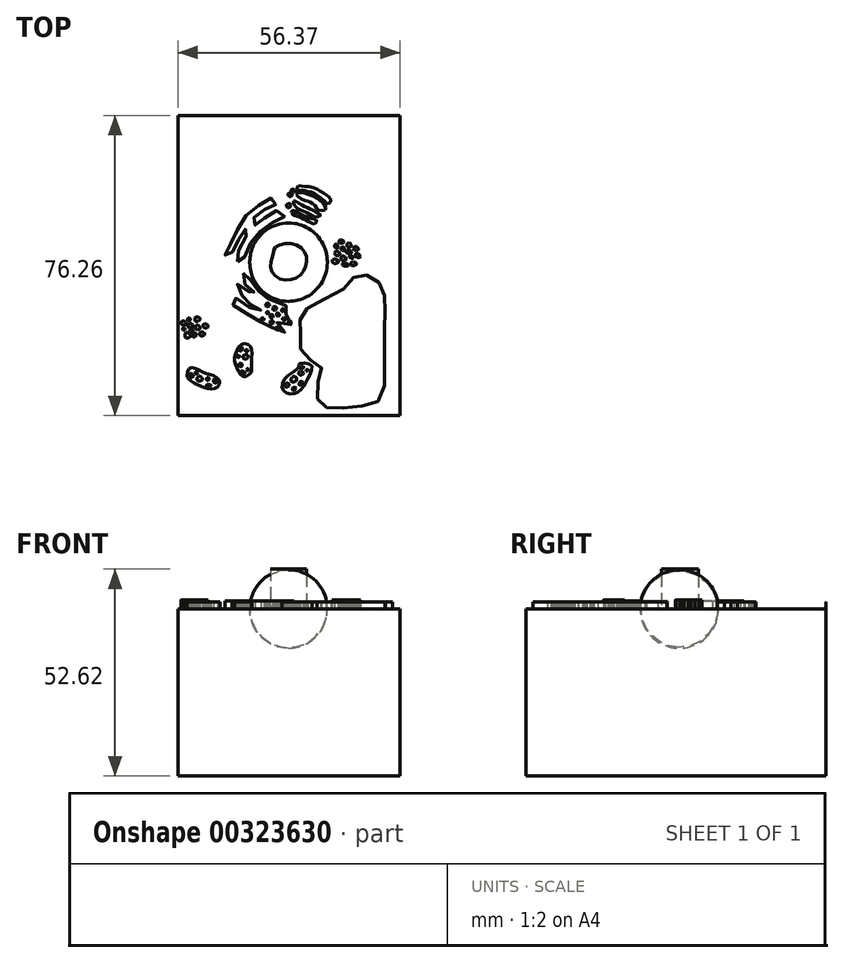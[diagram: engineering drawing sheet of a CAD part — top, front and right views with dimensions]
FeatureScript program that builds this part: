
annotation { "Feature Type Name" : "Feature", "Feature Type Description" : "" }
export const myFeature = defineFeature(function(context is Context, id is Id, definition is map)
    precondition{}
    {
        {
            var Q0;
            Q0=qCreatedBy(makeId("Front.planeOp"),FACE);
            var sketch = newSketch(context, id + "F0", { "sketchPlane" : qUnion([Q0])});
            skLineSegment(sketch, "E0", {"start": v(0, 0) * mm, "end": v(56.37, 0) * mm});
            skLineSegment(sketch, "E1", {"start": v(56.37, 0) * mm, "end": v(56.37, 42.46) * mm});
            skLineSegment(sketch, "E2", {"start": v(56.37, 42.46) * mm, "end": v(0, 42.46) * mm});
            skLineSegment(sketch, "E3", {"start": v(0, 42.46) * mm, "end": v(0, 0) * mm});
            skSolve(sketch);
        }
        {
            var Q0;
            Q0 = qSketchRegion(id + "F0", true);
            extrude(context, id + "F1", {"entities" : qUnion([Q0]), "depth" : 76.2 * mm});
        }
        {
            var Q0;
            Q0=makeQuery(id+"F1.opExtrude","SWEPT_FACE",FACE,{"disambiguationData":[OSD([sQuery(id+"F0.wireOp",EDGE,"E2")])]});
            var sketch = newSketch(context, id + "F2", { "sketchPlane" : qUnion([Q0])});
            skLineSegment(sketch, "E4", {"start": v(18.2, -37.24) * mm, "end": v(37.91, -37.24) * mm});
            skArc(sketch, "E5", {"start": v(37.91, -37.24) * mm, "mid": v(28.06, -27.5) * mm, "end": v(18.2, -37.24) * mm});
            skSolve(sketch);
        }
        {
            var Q0;
            Q0 = qSketchRegion(id + "F2", true);
            var Q1;
            Q1=sQuery(id+"F2.wireOp",EDGE,"E4");
            revolve(context, id + "F3", {"entities" : qUnion([Q0]), "axis" : qUnion([Q1]), "revolveType" : RevolveType.FULL});
        }
        {
            var Q0;
            Q0=makeQuery(id+"F1.opExtrude","SWEPT_FACE",FACE,{"disambiguationData":[OSD([sQuery(id+"F0.wireOp",EDGE,"E2")])]});
            var sketch = newSketch(context, id + "F4", { "sketchPlane" : qUnion([Q0])});
            skLineSegment(sketch, "E6", {"start": v(23.53, -36.84) * mm, "end": v(33.16, -36.84) * mm});
            skArc(sketch, "E7", {"start": v(33.16, -36.84) * mm, "mid": v(28.34, -32.03) * mm, "end": v(23.53, -36.84) * mm});
            skSolve(sketch);
        }
        {
            var Q0;
            Q0=sQuery(id+"F4.wireOp",EDGE,"E6");
            var Q1;
            Q1=sQuery(id+"F4.wireOp",EDGE,"E7");
            var Q2;
            Q2=makeQuery(id+"F3.opRevolve","SWEPT_FACE",FACE,{"disambiguationData":[OSD([sQuery(id+"F2.wireOp",EDGE,"E5")])]});
            revolve(context, id + "F5", {"bodyType" : ToolBodyType.SURFACE, "surfaceEntities" : qUnion([Q0, Q1]), "axis" : qUnion([Q2]), "revolveType" : RevolveType.FULL});
        }
        {
            var Q0;
            Q0=makeQuery(id+"F1.opExtrude","SWEPT_FACE",FACE,{"disambiguationData":[OSD([sQuery(id+"F0.wireOp",EDGE,"E2")])]});
            var sketch = newSketch(context, id + "F6", { "sketchPlane" : qUnion([Q0])});
            skFitSpline(sketch, "E8", {"points": [v(31.3, -19.52) * mm, v(34.38, -20.54) * mm, v(36.71, -22.14) * mm, v(37.51, -23.8) * mm, v(35.92, -24.05) * mm, v(34.75, -22.9) * mm, v(33.42, -21.92) * mm, v(31.77, -21.36) * mm, v(30.08, -19.97) * mm, v(30.5, -19.6) * mm, v(31.3, -19.52) * mm]});
            skFitSpline(sketch, "E9", {"points": [v(29.34, -21.68) * mm, v(31.26, -22.56) * mm, v(33.27, -23.6) * mm, v(35.23, -24.57) * mm, v(36.13, -25.3) * mm, v(35.33, -25.73) * mm, v(33.38, -25.13) * mm, v(32.04, -24.33) * mm, v(30.14, -23.49) * mm, v(29.34, -21.68) * mm]});
            skFitSpline(sketch, "E10", {"points": [v(29.72, -24.3) * mm, v(32.06, -25.46) * mm, v(34.16, -26.22) * mm, v(35.13, -26.54) * mm, v(34.7, -27.46) * mm, v(32.96, -26.83) * mm, v(30.75, -25.78) * mm, v(28.88, -24.77) * mm, v(28.96, -24.15) * mm, v(29.72, -24.3) * mm]});
            skFitSpline(sketch, "E11", {"points": [v(28.03, -19.78) * mm, v(28.28, -20.58) * mm, v(28.97, -20.07) * mm, v(28.03, -19.78) * mm]});
            skFitSpline(sketch, "E12", {"points": [v(27.61, -22.56) * mm, v(28.58, -22.53) * mm, v(28.3, -23.34) * mm, v(27.65, -23.2) * mm, v(27.61, -22.56) * mm]});
            skSolve(sketch);
        }
        {
            var Q0;
            Q0=makeQuery(id+"F6.imprint","IMPRINT",FACE,{"disambiguationData":[TD([[makeQuery(id+"F6.imprint","IMPRINT",EDGE,{"derivedFrom":sQuery(id+"F6.wireOp",EDGE,"E8")}),-1.0]])]});
            var Q1;
            Q1=makeQuery(id+"F6.imprint","IMPRINT",FACE,{"disambiguationData":[TD([[makeQuery(id+"F6.imprint","IMPRINT",EDGE,{"derivedFrom":sQuery(id+"F6.wireOp",EDGE,"E11")}),1.0]])]});
            var Q2;
            Q2=makeQuery(id+"F6.imprint","IMPRINT",FACE,{"disambiguationData":[TD([[makeQuery(id+"F6.imprint","IMPRINT",EDGE,{"derivedFrom":sQuery(id+"F6.wireOp",EDGE,"E10")}),-1.0]])]});
            var Q3;
            Q3=makeQuery(id+"F6.imprint","IMPRINT",FACE,{"disambiguationData":[TD([[makeQuery(id+"F6.imprint","IMPRINT",EDGE,{"derivedFrom":sQuery(id+"F6.wireOp",EDGE,"E9")}),-1.0]])]});
            var Q4;
            Q4=makeQuery(id+"F6.imprint","IMPRINT",FACE,{"disambiguationData":[TD([[makeQuery(id+"F6.imprint","IMPRINT",EDGE,{"derivedFrom":sQuery(id+"F6.wireOp",EDGE,"E12")}),-1.0]])]});
            extrude(context, id + "F7", {"entities" : qUnion([Q0, Q1, Q2, Q3, Q4]), "operationType" : NewBodyOperationType.ADD, "depth" : 1.78 * mm});
        }
        {
            var Q0;
            Q0=makeQuery(id+"F1.opExtrude","SWEPT_FACE",FACE,{"disambiguationData":[OSD([sQuery(id+"F0.wireOp",EDGE,"E2")])]});
            var sketch = newSketch(context, id + "F8", { "sketchPlane" : qUnion([Q0])});
            skFitSpline(sketch, "E13", {"points": [v(2.83, -64.3) * mm, v(2.4, -66.39) * mm, v(3.72, -67.72) * mm, v(5.38, -68.57) * mm, v(7.66, -69.4) * mm, v(9.46, -69.28) * mm, v(10.62, -67.74) * mm, v(9.1, -66.1) * mm, v(6.66, -65.34) * mm, v(4.44, -64.22) * mm, v(2.83, -64.3) * mm]});
            skFitSpline(sketch, "E14", {"points": [v(3.1, -65.6) * mm, v(3.22, -66.46) * mm, v(3.92, -66.02) * mm, v(3.48, -65.63) * mm, v(3.1, -65.6) * mm]});
            skFitSpline(sketch, "E15", {"points": [v(5.34, -66.2) * mm, v(4.77, -67.1) * mm, v(5.58, -67.42) * mm, v(6.18, -66.88) * mm, v(5.34, -66.2) * mm]});
            skFitSpline(sketch, "E16", {"points": [v(7.3, -66.67) * mm, v(7.3, -67.22) * mm, v(7.87, -67.02) * mm, v(7.71, -66.56) * mm, v(7.3, -66.67) * mm]});
            skFitSpline(sketch, "E17", {"points": [v(7.18, -68.5) * mm, v(7.77, -68.98) * mm, v(8.33, -68.56) * mm, v(7.8, -68.27) * mm, v(7.18, -68.5) * mm]});
            skFitSpline(sketch, "E18", {"points": [v(9.23, -66.88) * mm, v(9.02, -67.65) * mm, v(9.68, -67.88) * mm, v(9.97, -67.49) * mm, v(9.23, -66.88) * mm]});
            skFitSpline(sketch, "E19", {"points": [v(4.46, -65.05) * mm, v(4.57, -65.6) * mm, v(5.02, -65.33) * mm, v(4.77, -65.04) * mm, v(4.46, -65.05) * mm]});
            skFitSpline(sketch, "E20", {"points": [v(30.66, -63.92) * mm, v(27.48, -66.45) * mm, v(26.61, -69.5) * mm, v(28.81, -70.7) * mm, v(31.28, -69.48) * mm, v(33.02, -66.64) * mm, v(33.78, -63.35) * mm, v(30.7, -63.13) * mm, v(30.66, -63.92) * mm]});
            skFitSpline(sketch, "E21", {"points": [v(27.32, -68.2) * mm, v(27.35, -68.96) * mm, v(28.19, -68.62) * mm, v(27.85, -67.95) * mm, v(27.32, -68.2) * mm]});
            skFitSpline(sketch, "E22", {"points": [v(28.93, -66.47) * mm, v(28.82, -67.5) * mm, v(29.9, -67.45) * mm, v(30, -66.49) * mm, v(28.93, -66.47) * mm]});
            skFitSpline(sketch, "E23", {"points": [v(29.3, -69.83) * mm, v(29.91, -69.13) * mm, v(29.17, -69.16) * mm, v(29.06, -69.7) * mm, v(29.3, -69.83) * mm]});
            skFitSpline(sketch, "E24", {"points": [v(30.95, -67.67) * mm, v(30.86, -68.46) * mm, v(31.67, -68.1) * mm, v(31.42, -67.53) * mm, v(30.95, -67.67) * mm]});
            skFitSpline(sketch, "E25", {"points": [v(16.06, -58.2) * mm, v(14.67, -60.31) * mm, v(14.38, -62.5) * mm, v(15.41, -64.97) * mm, v(16.66, -66.29) * mm, v(18.52, -65.34) * mm, v(18.58, -63.17) * mm, v(18.77, -60.38) * mm, v(18.05, -58.27) * mm, v(16.06, -58.2) * mm]});
            skFitSpline(sketch, "E26", {"points": [v(15.76, -59.01) * mm, v(15.53, -59.64) * mm, v(16.1, -59.68) * mm, v(16.39, -59.1) * mm, v(15.76, -59.01) * mm]});
            skFitSpline(sketch, "E27", {"points": [v(17.36, -59.46) * mm, v(17.14, -59.85) * mm, v(17.71, -59.79) * mm, v(17.36, -59.46) * mm]});
            skFitSpline(sketch, "E28", {"points": [v(15.08, -60.93) * mm, v(15.12, -61.37) * mm, v(15.66, -61.2) * mm, v(15.08, -60.93) * mm]});
            skFitSpline(sketch, "E29", {"points": [v(17.03, -60.75) * mm, v(16.43, -61.42) * mm, v(16.89, -61.85) * mm, v(17.63, -61.6) * mm, v(17.78, -60.93) * mm, v(17.03, -60.75) * mm]});
            skFitSpline(sketch, "E30", {"points": [v(15.45, -63.06) * mm, v(16.28, -63.18) * mm, v(15.9, -63.77) * mm, v(15.45, -63.06) * mm]});
            skFitSpline(sketch, "E31", {"points": [v(17.58, -64.2) * mm, v(17.53, -64.73) * mm, v(17.97, -64.65) * mm, v(17.58, -64.2) * mm]});
            skFitSpline(sketch, "E32", {"points": [v(15.99, -64.92) * mm, v(16.15, -65.6) * mm, v(17, -65.35) * mm, v(15.99, -64.92) * mm]});
            skFitSpline(sketch, "E33", {"points": [v(30.95, -64.97) * mm, v(30.78, -65.78) * mm, v(31.82, -65.53) * mm, v(30.95, -64.97) * mm]});
            skFitSpline(sketch, "E34", {"points": [v(32.78, -64.46) * mm, v(32.56, -64.86) * mm, v(33.06, -64.73) * mm, v(32.78, -64.46) * mm]});
            skFitSpline(sketch, "E35", {"points": [v(31.32, -63.72) * mm, v(31.1, -64.27) * mm, v(31.93, -64.02) * mm, v(31.32, -63.72) * mm]});
            skSolve(sketch);
        }
        {
            var Q0;
            Q0 = qSketchRegion(id + "F8", true);
            extrude(context, id + "F9", {"entities" : qUnion([Q0]), "operationType" : NewBodyOperationType.ADD, "depth" : 1.78 * mm});
        }
        {
            var Q0;
            {var subQ1=sQuery(id+"F0.wireOp",EDGE,"E2");var subQ2=sQuery(id+"F0.wireOp",EDGE,"E1");Q0=makeQuery(id+"F9.boolean.opBoolean","SPLIT",FACE,{"disambiguationData":[TD([makeQuery(id+"F1.opExtrude","SWEPT_FACE",FACE,{"disambiguationData":[OSD([subQ2])]})])],"derivedFrom":makeQuery(id+"F1.opExtrude","SWEPT_FACE",FACE,{"disambiguationData":[OSD([subQ1])]})});}
            var sketch = newSketch(context, id + "F10", { "sketchPlane" : qUnion([Q0])});
            skFitSpline(sketch, "E36", {"points": [v(27.47, -50.37) * mm, v(28.2, -49.17) * mm, v(28.12, -48.16) * mm, v(26.8, -48.59) * mm, v(25.74, -48.68) * mm, v(25.5, -48.16) * mm, v(25.63, -47.5) * mm, v(24.86, -47.37) * mm, v(23.2, -46.81) * mm, v(22.66, -46.21) * mm, v(21.56, -45.4) * mm, v(20.63, -44.72) * mm, v(19.42, -43.5) * mm, v(18.64, -42.5) * mm, v(18.38, -41.47) * mm, v(17.9, -40.74) * mm, v(17.1, -40.1) * mm, v(16.55, -40.23) * mm, v(16.22, -40.98) * mm, v(16.46, -42.12) * mm, v(17.53, -43.19) * mm, v(18.47, -43.48) * mm, v(19.06, -44.67) * mm, v(19.59, -45.3) * mm, v(18.87, -45.96) * mm, v(17.95, -44.74) * mm, v(16.21, -43.7) * mm, v(15.38, -42.7) * mm, v(14.56, -43.76) * mm, v(15.46, -45.02) * mm, v(16.83, -46.19) * mm, v(17.94, -47.4) * mm, v(18.13, -47.86) * mm, v(19.5, -48.17) * mm, v(20.7, -48.36) * mm, v(20.95, -49.63) * mm, v(19.82, -50.39) * mm, v(18.34, -48.9) * mm, v(16.22, -47.83) * mm, v(14.73, -46.46) * mm, v(14.02, -45.55) * mm, v(13.72, -47.46) * mm, v(15.07, -48.9) * mm, v(16.73, -49.62) * mm, v(18.6, -51.47) * mm, v(20.61, -52.54) * mm, v(22.01, -52.3) * mm, v(23.11, -53.17) * mm, v(24.1, -54.15) * mm, v(25.64, -55.27) * mm, v(27.06, -55.02) * mm, v(26.22, -53.87) * mm, v(24.87, -52.75) * mm, v(26.37, -52.59) * mm, v(27.7, -53.01) * mm, v(28.9, -52.99) * mm, v(29.37, -51.91) * mm, v(27.47, -50.37) * mm]});
            skFitSpline(sketch, "E37", {"points": [v(25, -50.23) * mm, v(25.73, -50.45) * mm, v(25.37, -51) * mm, v(25, -50.23) * mm]});
            skFitSpline(sketch, "E38", {"points": [v(26.6, -51.4) * mm, v(26.78, -52.02) * mm, v(27.35, -51.69) * mm, v(26.6, -51.4) * mm]});
            skFitSpline(sketch, "E39", {"points": [v(23.4, -52.26) * mm, v(23.65, -52.93) * mm, v(24.19, -52.36) * mm, v(23.4, -52.26) * mm]});
            skFitSpline(sketch, "E40", {"points": [v(24.06, -51.25) * mm, v(23.83, -50.57) * mm, v(23.33, -51.17) * mm, v(24.06, -51.25) * mm]});
            skFitSpline(sketch, "E41", {"points": [v(26.6, -49.07) * mm, v(26.32, -49.61) * mm, v(26.96, -49.8) * mm, v(26.85, -49.26) * mm, v(26.6, -49.07) * mm]});
            skFitSpline(sketch, "E42", {"points": [v(24.82, -53.84) * mm, v(24.99, -54.41) * mm, v(25.59, -54.15) * mm, v(24.82, -53.84) * mm]});
            skFitSpline(sketch, "E43", {"points": [v(24.58, -48.45) * mm, v(24.09, -49.28) * mm, v(25, -49.1) * mm, v(24.58, -48.45) * mm]});
            skFitSpline(sketch, "E44", {"points": [v(22.74, -49.75) * mm, v(22.5, -50.26) * mm, v(23, -50.16) * mm, v(22.74, -49.75) * mm]});
            skFitSpline(sketch, "E45", {"points": [v(21.24, -51.47) * mm, v(21.17, -51.93) * mm, v(21.89, -51.7) * mm, v(21.24, -51.47) * mm]});
            skFitSpline(sketch, "E46", {"points": [v(22.8, -47.58) * mm, v(22.27, -48.29) * mm, v(23.16, -48.4) * mm, v(22.8, -47.58) * mm]});
            skFitSpline(sketch, "E47", {"points": [v(28.2, -52.13) * mm, v(28.2, -52.59) * mm, v(28.73, -52.44) * mm, v(28.2, -52.13) * mm]});
            skSolve(sketch);
        }
        {
            var Q0;
            Q0 = qSketchRegion(id + "F10", true);
            extrude(context, id + "F11", {"entities" : qUnion([Q0]), "operationType" : NewBodyOperationType.ADD, "depth" : 2.03 * mm});
        }
        {
            var Q0;
            {var subQ6=sQuery(id+"F0.wireOp",EDGE,"E2");var subQ7=sQuery(id+"F0.wireOp",EDGE,"E1");var subQ12=makeQuery(id+"F1.opExtrude","SWEPT_FACE",FACE,{"disambiguationData":[OSD([subQ7])]});Q0=makeQuery(id+"F11.boolean.opBoolean","SPLIT",FACE,{"disambiguationData":[TD([subQ12])],"derivedFrom":makeQuery(id+"F9.boolean.opBoolean","SPLIT",FACE,{"disambiguationData":[TD([subQ12])],"derivedFrom":makeQuery(id+"F1.opExtrude","SWEPT_FACE",FACE,{"disambiguationData":[OSD([subQ6])]})})});}
            var sketch = newSketch(context, id + "F12", { "sketchPlane" : qUnion([Q0])});
            skFitSpline(sketch, "E48", {"points": [v(40.12, -32.66) * mm, v(39.83, -33.41) * mm, v(40.65, -33.51) * mm, v(40.12, -32.66) * mm]});
            skFitSpline(sketch, "E49", {"points": [v(40.07, -34.4) * mm, v(40, -35.49) * mm, v(41.12, -35.19) * mm, v(40.07, -34.4) * mm]});
            skFitSpline(sketch, "E50", {"points": [v(41.75, -33.37) * mm, v(41.44, -34.06) * mm, v(42.34, -34.14) * mm, v(41.75, -33.37) * mm]});
            skFitSpline(sketch, "E51", {"points": [v(41.14, -31.56) * mm, v(41.02, -32.31) * mm, v(42.09, -32.15) * mm, v(41.14, -31.56) * mm]});
            skFitSpline(sketch, "E52", {"points": [v(43.4, -32.3) * mm, v(42.92, -33.18) * mm, v(43.9, -33.19) * mm, v(43.4, -32.3) * mm]});
            skFitSpline(sketch, "E53", {"points": [v(43.08, -34.15) * mm, v(42.76, -34.83) * mm, v(44.1, -34.89) * mm, v(43.08, -34.15) * mm]});
            skFitSpline(sketch, "E54", {"points": [v(41.86, -35.72) * mm, v(41.42, -36.57) * mm, v(42.7, -36.5) * mm, v(41.86, -35.72) * mm]});
            skFitSpline(sketch, "E55", {"points": [v(44.59, -36.17) * mm, v(43.66, -35.57) * mm, v(43.65, -36.01) * mm, v(44.59, -36.17) * mm]});
            skFitSpline(sketch, "E56", {"points": [v(45.01, -33.23) * mm, v(44.56, -34) * mm, v(45.8, -34) * mm, v(45.01, -33.23) * mm]});
            skFitSpline(sketch, "E57", {"points": [v(39.28, -36.6) * mm, v(39.6, -37.55) * mm, v(40.76, -36.97) * mm, v(39.28, -36.6) * mm]});
            skFitSpline(sketch, "E58", {"points": [v(45.19, -34.98) * mm, v(45.3, -35.88) * mm, v(46.3, -35.83) * mm, v(45.19, -34.98) * mm]});
            skFitSpline(sketch, "E59", {"points": [v(41.88, -37.5) * mm, v(41.97, -38.11) * mm, v(43.29, -37.98) * mm, v(41.88, -37.5) * mm]});
            skFitSpline(sketch, "E60", {"points": [v(44.25, -37.17) * mm, v(44, -38.05) * mm, v(45.32, -37.7) * mm, v(44.25, -37.17) * mm]});
            skFitSpline(sketch, "E61", {"points": [v(2.93, -52.8) * mm, v(2.62, -53.79) * mm, v(3.8, -53.38) * mm, v(2.93, -52.8) * mm]});
            skFitSpline(sketch, "E62", {"points": [v(4.91, -53.2) * mm, v(4.49, -54.22) * mm, v(5.53, -54.15) * mm, v(4.91, -53.2) * mm]});
            skFitSpline(sketch, "E63", {"points": [v(2.03, -55.1) * mm, v(2, -56.46) * mm, v(3.15, -55.94) * mm, v(2.03, -55.1) * mm]});
            skFitSpline(sketch, "E64", {"points": [v(4.06, -55.2) * mm, v(3.75, -56.19) * mm, v(4.68, -55.67) * mm, v(4.06, -55.2) * mm]});
            skFitSpline(sketch, "E65", {"points": [v(5.95, -54.92) * mm, v(5.53, -55.8) * mm, v(6.74, -55.65) * mm, v(5.95, -54.92) * mm]});
            skFitSpline(sketch, "E66", {"points": [v(6.72, -52.9) * mm, v(6.46, -53.77) * mm, v(7.65, -53.59) * mm, v(6.72, -52.9) * mm]});
            skFitSpline(sketch, "E67", {"points": [v(5.6, -51.66) * mm, v(4.52, -51.2) * mm, v(4.46, -52.24) * mm, v(5.6, -51.66) * mm]});
            skFitSpline(sketch, "E68", {"points": [v(2.66, -51.4) * mm, v(2.52, -52) * mm, v(3.16, -51.83) * mm, v(2.66, -51.4) * mm]});
            skFitSpline(sketch, "E69", {"points": [v(1.34, -53.92) * mm, v(1.2, -54.4) * mm, v(1.78, -54.25) * mm, v(1.34, -53.92) * mm]});
            skFitSpline(sketch, "E70", {"points": [v(1.05, -52.22) * mm, v(0.79, -52.9) * mm, v(1.96, -53.12) * mm, v(1.84, -52.45) * mm, v(1.05, -52.22) * mm]});
            skFitSpline(sketch, "E71", {"points": [v(3.04, -54.42) * mm, v(3.13, -54.93) * mm, v(3.62, -54.83) * mm, v(3.8, -54.3) * mm, v(3.19, -54.37) * mm, v(3.04, -54.42) * mm]});
            skSolve(sketch);
        }
        {
            var Q0;
            Q0 = qSketchRegion(id + "F12", true);
            extrude(context, id + "F13", {"entities" : qUnion([Q0]), "operationType" : NewBodyOperationType.ADD, "depth" : 2.3 * mm});
        }
        {
            var Q0;
            {var subQ6=sQuery(id+"F0.wireOp",EDGE,"E2");var subQ7=sQuery(id+"F0.wireOp",EDGE,"E1");var subQ12=makeQuery(id+"F1.opExtrude","SWEPT_FACE",FACE,{"disambiguationData":[OSD([subQ7])]});Q0=makeQuery(id+"F11.boolean.opBoolean","SPLIT",FACE,{"disambiguationData":[TD([subQ12])],"derivedFrom":makeQuery(id+"F9.boolean.opBoolean","SPLIT",FACE,{"disambiguationData":[TD([subQ12])],"derivedFrom":makeQuery(id+"F1.opExtrude","SWEPT_FACE",FACE,{"disambiguationData":[OSD([subQ6])]})})});}
            var sketch = newSketch(context, id + "F14", { "sketchPlane" : qUnion([Q0])});
            skFitSpline(sketch, "E72", {"points": [v(24.24, -34.7) * mm, v(23.53, -38.43) * mm, v(25.9, -41.47) * mm, v(30.2, -41.08) * mm, v(32.44, -38.2) * mm, v(32.1, -34.6) * mm, v(28.27, -32.4) * mm, v(24.55, -33.57) * mm, v(24.24, -34.7) * mm]});
            skSolve(sketch);
        }
        {
            var Q0;
            Q0 = qSketchRegion(id + "F14", true);
            extrude(context, id + "F15", {"entities" : qUnion([Q0]), "depth" : 10.16 * mm});
        }
        {
            var Q0;
            {var subQ6=sQuery(id+"F0.wireOp",EDGE,"E2");var subQ7=sQuery(id+"F0.wireOp",EDGE,"E1");var subQ12=makeQuery(id+"F1.opExtrude","SWEPT_FACE",FACE,{"disambiguationData":[OSD([subQ7])]});Q0=makeQuery(id+"F11.boolean.opBoolean","SPLIT",FACE,{"disambiguationData":[TD([subQ12])],"derivedFrom":makeQuery(id+"F9.boolean.opBoolean","SPLIT",FACE,{"disambiguationData":[TD([subQ12])],"derivedFrom":makeQuery(id+"F1.opExtrude","SWEPT_FACE",FACE,{"disambiguationData":[OSD([subQ6])]})})});}
            var sketch = newSketch(context, id + "F16", { "sketchPlane" : qUnion([Q0])});
            skFitSpline(sketch, "E73", {"points": [v(41.96, -44.04) * mm, v(33.46, -48.45) * mm, v(31.02, -51.84) * mm, v(31.12, -55.86) * mm, v(31.77, -60.77) * mm, v(36.25, -63.66) * mm, v(35.78, -66.89) * mm, v(35.72, -72.74) * mm, v(39.08, -74.3) * mm, v(46.3, -73.87) * mm, v(51.56, -71.78) * mm, v(52.49, -62.71) * mm, v(52.4, -55.8) * mm, v(52.59, -49.86) * mm, v(52.2, -44.4) * mm, v(49.45, -41.18) * mm, v(45.26, -40.68) * mm, v(41.96, -44.04) * mm]});
            skSolve(sketch);
        }
        {
            var Q0;
            Q0 = qSketchRegion(id + "F16", true);
            extrude(context, id + "F17", {"entities" : qUnion([Q0]), "operationType" : NewBodyOperationType.ADD, "depth" : 1.78 * mm});
        }
        {
            var Q0;
            {var subQ6=sQuery(id+"F0.wireOp",EDGE,"E2");var subQ7=sQuery(id+"F0.wireOp",EDGE,"E1");var subQ12=makeQuery(id+"F1.opExtrude","SWEPT_FACE",FACE,{"disambiguationData":[OSD([subQ7])]});Q0=makeQuery(id+"F11.boolean.opBoolean","SPLIT",FACE,{"disambiguationData":[TD([subQ12])],"derivedFrom":makeQuery(id+"F9.boolean.opBoolean","SPLIT",FACE,{"disambiguationData":[TD([subQ12])],"derivedFrom":makeQuery(id+"F1.opExtrude","SWEPT_FACE",FACE,{"disambiguationData":[OSD([subQ6])]})})});}
            var sketch = newSketch(context, id + "F18", { "sketchPlane" : qUnion([Q0])});
            skFitSpline(sketch, "E74", {"points": [v(45.68, -22.6) * mm, v(42.36, -22.61) * mm, v(40.35, -22.98) * mm, v(39.1, -24.56) * mm, v(39.7, -26.6) * mm, v(42.43, -27.64) * mm, v(45.03, -27.62) * mm, v(46.53, -27.49) * mm, v(48.06, -28.23) * mm, v(48.86, -29.1) * mm, v(50.42, -29.77) * mm, v(52, -30.08) * mm, v(53.44, -30.17) * mm, v(54.62, -29.05) * mm, v(55.17, -26.04) * mm, v(53.1, -24.4) * mm, v(50.8, -24.07) * mm, v(48, -23.26) * mm, v(45.68, -22.6) * mm]});
            skFitSpline(sketch, "E75", {"points": [v(41.15, -23.98) * mm, v(40.5, -23.96) * mm, v(40.28, -24.56) * mm, v(40.19, -25.26) * mm, v(40.27, -26) * mm, v(40.95, -26.23) * mm, v(41.35, -25.95) * mm, v(41.3, -25.41) * mm, v(41.5, -25.07) * mm, v(41.74, -24.91) * mm, v(41.88, -25.28) * mm, v(41.86, -25.89) * mm, v(41.84, -26.49) * mm, v(41.9, -26.9) * mm, v(42.38, -26.93) * mm, v(42.63, -26.45) * mm, v(42.74, -25.8) * mm, v(42.87, -25.09) * mm, v(43.32, -25.27) * mm, v(43.42, -25.79) * mm, v(43.44, -26.38) * mm, v(43.64, -26.96) * mm, v(44.14, -26.69) * mm, v(44.34, -25.82) * mm, v(44.54, -25.3) * mm, v(45.12, -25.44) * mm, v(45.24, -26.13) * mm, v(45.26, -26.83) * mm, v(45.7, -26.96) * mm, v(46.3, -26.35) * mm, v(46.5, -25.73) * mm, v(46.86, -25.71) * mm, v(47.05, -26.2) * mm, v(46.97, -26.9) * mm, v(47.45, -27.28) * mm, v(47.7, -27.1) * mm, v(47.89, -26.46) * mm, v(48.12, -25.77) * mm, v(48.31, -25.62) * mm, v(48.63, -25.9) * mm, v(48.58, -26.43) * mm, v(48.51, -27.34) * mm, v(48.55, -27.93) * mm, v(48.9, -28.16) * mm, v(49.35, -27.72) * mm, v(49.7, -27.19) * mm, v(49.9, -26.71) * mm, v(49.99, -26.31) * mm, v(50.49, -26.59) * mm, v(50.4, -27.28) * mm, v(50.25, -28.04) * mm, v(49.92, -28.77) * mm, v(50.26, -29.08) * mm, v(50.74, -29) * mm, v(51.01, -28.25) * mm, v(51.33, -27.47) * mm, v(51.55, -26.93) * mm, v(51.94, -27.5) * mm, v(51.96, -28.03) * mm, v(51.74, -28.82) * mm, v(51.89, -29.33) * mm, v(52.62, -29.33) * mm, v(53.05, -28.12) * mm, v(53.23, -26.92) * mm, v(53.38, -26.1) * mm, v(53, -25.56) * mm, v(52.06, -24.94) * mm, v(51.8, -25.41) * mm, v(51.33, -25.81) * mm, v(51.14, -25.12) * mm, v(50.65, -24.53) * mm, v(49.94, -24.78) * mm, v(49.71, -25.6) * mm, v(49.28, -25.47) * mm, v(49.24, -24.54) * mm, v(48.8, -24.22) * mm, v(48.26, -24.44) * mm, v(47.87, -25.16) * mm, v(47.2, -24.6) * mm, v(47.08, -23.66) * mm, v(46.16, -23.65) * mm, v(46.07, -24.54) * mm, v(46.02, -25.04) * mm, v(45.46, -24.82) * mm, v(45.4, -23.9) * mm, v(45.3, -23.25) * mm, v(44.56, -23.27) * mm, v(44.3, -23.95) * mm, v(44.29, -24.56) * mm, v(43.78, -24.44) * mm, v(43.4, -23.61) * mm, v(43.16, -23.18) * mm, v(42.46, -23.34) * mm, v(42.3, -24.25) * mm, v(41.76, -24.19) * mm, v(41.15, -23.98) * mm]});
            skSolve(sketch);
        }
        {
            var Q0;
            Q0=sQuery(id+"F18.wireOp",EDGE,"E75");
            var Q1;
            Q1=sQuery(id+"F18.wireOp",EDGE,"E74");
            extrude(context, id + "F19", {"bodyType" : ToolBodyType.SURFACE, "surfaceEntities" : qUnion([Q0, Q1]), "depth" : 1.78 * mm});
        }
        {
            var Q0;
            {var subQ6=sQuery(id+"F0.wireOp",EDGE,"E2");var subQ7=sQuery(id+"F0.wireOp",EDGE,"E1");var subQ12=makeQuery(id+"F1.opExtrude","SWEPT_FACE",FACE,{"disambiguationData":[OSD([subQ7])]});Q0=makeQuery(id+"F11.boolean.opBoolean","SPLIT",FACE,{"disambiguationData":[TD([subQ12])],"derivedFrom":makeQuery(id+"F9.boolean.opBoolean","SPLIT",FACE,{"disambiguationData":[TD([subQ12])],"derivedFrom":makeQuery(id+"F1.opExtrude","SWEPT_FACE",FACE,{"disambiguationData":[OSD([subQ6])]})})});}
            var sketch = newSketch(context, id + "F20", { "sketchPlane" : qUnion([Q0])});
            skFitSpline(sketch, "E76", {"points": [v(15.17, -37.04) * mm, v(16.26, -37.7) * mm, v(16.97, -35.7) * mm, v(17.77, -33.43) * mm, v(18.96, -31.52) * mm, v(20.4, -29.68) * mm, v(22.66, -28.21) * mm, v(24.29, -26.92) * mm, v(26.07, -26.29) * mm, v(27.15, -25.22) * mm, v(26.04, -24.16) * mm, v(24.47, -24.34) * mm, v(22.9, -25.5) * mm, v(20.85, -26.78) * mm, v(20, -27.86) * mm, v(18.83, -27.27) * mm, v(18.74, -26.3) * mm, v(19.52, -25.75) * mm, v(20.9, -24.57) * mm, v(22.52, -23.56) * mm, v(23.8, -22.9) * mm, v(24.94, -22.47) * mm, v(24.55, -21.06) * mm, v(23.64, -20.98) * mm, v(21.8, -21.91) * mm, v(20.07, -23.16) * mm, v(17.92, -24.82) * mm, v(16.03, -27.1) * mm, v(14.81, -29.44) * mm, v(13.8, -31.56) * mm, v(12.77, -33.44) * mm, v(11.95, -35.15) * mm, v(12.57, -36.32) * mm, v(13.65, -34.97) * mm, v(14.36, -33.16) * mm, v(15.46, -31.4) * mm, v(16.17, -30.04) * mm, v(17.18, -28.8) * mm, v(17.77, -29.1) * mm, v(17.63, -29.98) * mm, v(16.58, -32.1) * mm, v(15.3, -34.32) * mm, v(14.6, -35.73) * mm, v(15.17, -37.04) * mm]});
            skSolve(sketch);
        }
        {
            var Q0;
            Q0 = qSketchRegion(id + "F20", true);
            extrude(context, id + "F21", {"entities" : qUnion([Q0]), "operationType" : NewBodyOperationType.ADD, "depth" : 2.03 * mm});
        }
        {
            var Q0;
            {var subQ6=sQuery(id+"F0.wireOp",EDGE,"E2");var subQ7=sQuery(id+"F0.wireOp",EDGE,"E1");var subQ12=makeQuery(id+"F1.opExtrude","SWEPT_FACE",FACE,{"disambiguationData":[OSD([subQ7])]});Q0=makeQuery(id+"F11.boolean.opBoolean","SPLIT",FACE,{"disambiguationData":[TD([subQ12])],"derivedFrom":makeQuery(id+"F9.boolean.opBoolean","SPLIT",FACE,{"disambiguationData":[TD([subQ12])],"derivedFrom":makeQuery(id+"F1.opExtrude","SWEPT_FACE",FACE,{"disambiguationData":[OSD([subQ6])]})})});}
            var sketch = newSketch(context, id + "F22", { "sketchPlane" : qUnion([Q0])});
            skFitSpline(sketch, "E77", {"points": [v(0.8, -50.9) * mm, v(2.28, -50.23) * mm, v(2.44, -47.74) * mm, v(2.63, -44.73) * mm, v(2.13, -41.77) * mm, v(2, -37.43) * mm, v(2.13, -34.22) * mm, v(2.1, -31.06) * mm, v(2.38, -27.65) * mm, v(2.2, -24.14) * mm, v(2.28, -20.2) * mm, v(2.7, -16.85) * mm, v(2.35, -13.31) * mm, v(2.45, -9.07) * mm, v(2.57, -5.62) * mm, v(2.6, -3.35) * mm, v(3, -2.12) * mm, v(4.85, -2.52) * mm, v(7.24, -2.44) * mm, v(10.58, -1.97) * mm, v(13.27, -1.87) * mm, v(16.28, -1.81) * mm, v(19.82, -2.27) * mm, v(23, -2.12) * mm, v(26.51, -2.43) * mm, v(29.62, -2.25) * mm, v(34.1, -2) * mm, v(37.8, -2.22) * mm, v(40.17, -2.04) * mm, v(42.8, -2.52) * mm, v(45.13, -2.15) * mm, v(47.34, -1.63) * mm, v(49.94, -1.6) * mm, v(52.72, -1.98) * mm, v(54.62, -2.05) * mm, v(56.37, -2) * mm, v(55.6, -0.76) * mm, v(54.46, 0) * mm, v(52.71, 0) * mm, v(51.76, 0) * mm, v(48.94, 0) * mm, v(45.27, 0) * mm, v(40.7, 0) * mm, v(35.84, 0) * mm, v(30.96, 0) * mm, v(23.94, 0) * mm, v(17.06, 0) * mm, v(12.98, 0) * mm, v(7.86, 0) * mm, v(2.66, 0) * mm, v(0.9, -1.18) * mm, v(0, -3.2) * mm, v(0, -7.45) * mm, v(0, -14) * mm, v(0, -19.83) * mm, v(0, -24.98) * mm, v(0, -32.41) * mm, v(0, -36.93) * mm, v(0, -41.26) * mm, v(0, -46.38) * mm, v(0, -49.66) * mm, v(0.8, -50.9) * mm]});
            skSolve(sketch);
        }
        {
            var Q0;
            {var subQ0=sQuery(id+"F22.wireOp",EDGE,"E77");var subQ1=sQuery(id+"F0.wireOp",EDGE,"E2");var subQ14=makeQuery(id+"F1.opExtrude","CAP_EDGE",EDGE,{"disambiguationData":[OSD([subQ1])],"isStart":true});var subQ26=makeQuery(id+"F22.imprint","INTERSECT",VERTEX,{"disambiguationData":[OD(0.0)],"derivedFrom":[subQ14,subQ0]});Q0=makeQuery(id+"F22.imprint","IMPRINT",FACE,{"disambiguationData":[TD([[makeQuery(id+"F22.imprint","IMPRINT",EDGE,{"disambiguationData":[TD([[subQ26,-1.0]])],"derivedFrom":subQ0}),1.0]])]});}
            extrude(context, id + "F23", {"entities" : qUnion([Q0]), "operationType" : NewBodyOperationType.ADD, "depth" : 1.78 * mm});
        }
        {
            var Q0;
            {var subQ2=sQuery(id+"F0.wireOp",EDGE,"E2");var subQ4=makeQuery(id+"F7.opExtrude","SWEPT_FACE",FACE,{"disambiguationData":[OSD([sQuery(id+"F6.wireOp",EDGE,"E8")])]});var subQ10=sQuery(id+"F0.wireOp",EDGE,"E1");var subQ11=makeQuery(id+"F1.opExtrude","SWEPT_FACE",FACE,{"disambiguationData":[OSD([subQ10])]});Q0=makeQuery(id+"F23.boolean.opBoolean","SPLIT",FACE,{"disambiguationData":[TD([subQ4])],"derivedFrom":makeQuery(id+"F11.boolean.opBoolean","SPLIT",FACE,{"disambiguationData":[TD([subQ11])],"derivedFrom":makeQuery(id+"F9.boolean.opBoolean","SPLIT",FACE,{"disambiguationData":[TD([subQ11])],"derivedFrom":makeQuery(id+"F1.opExtrude","SWEPT_FACE",FACE,{"disambiguationData":[OSD([subQ2])]})})})});}
            var sketch = newSketch(context, id + "F24", { "sketchPlane" : qUnion([Q0])});
            skFitSpline(sketch, "E78", {"points": [v(30.65, -17.8) * mm, v(30.17, -18.92) * mm, v(31.2, -19) * mm, v(32.1, -19.02) * mm, v(33.26, -19.3) * mm, v(34.49, -19.68) * mm, v(35.61, -20.46) * mm, v(37.26, -21.72) * mm, v(38.04, -22.42) * mm, v(38.82, -21.65) * mm, v(38.37, -20.7) * mm, v(37.5, -20) * mm, v(36.02, -19.16) * mm, v(34.8, -18.44) * mm, v(32.94, -17.95) * mm, v(31.62, -18) * mm, v(30.65, -17.8) * mm]});
            skFitSpline(sketch, "E79", {"points": [v(28.76, -18.85) * mm, v(28.98, -19.43) * mm, v(29.67, -19.3) * mm, v(29.47, -18.8) * mm, v(28.76, -18.85) * mm]});
            skSolve(sketch);
        }
        {
            var Q0;
            Q0 = qSketchRegion(id + "F24", true);
            extrude(context, id + "F25", {"entities" : qUnion([Q0]), "operationType" : NewBodyOperationType.ADD, "depth" : 1.78 * mm});
        }
    });
